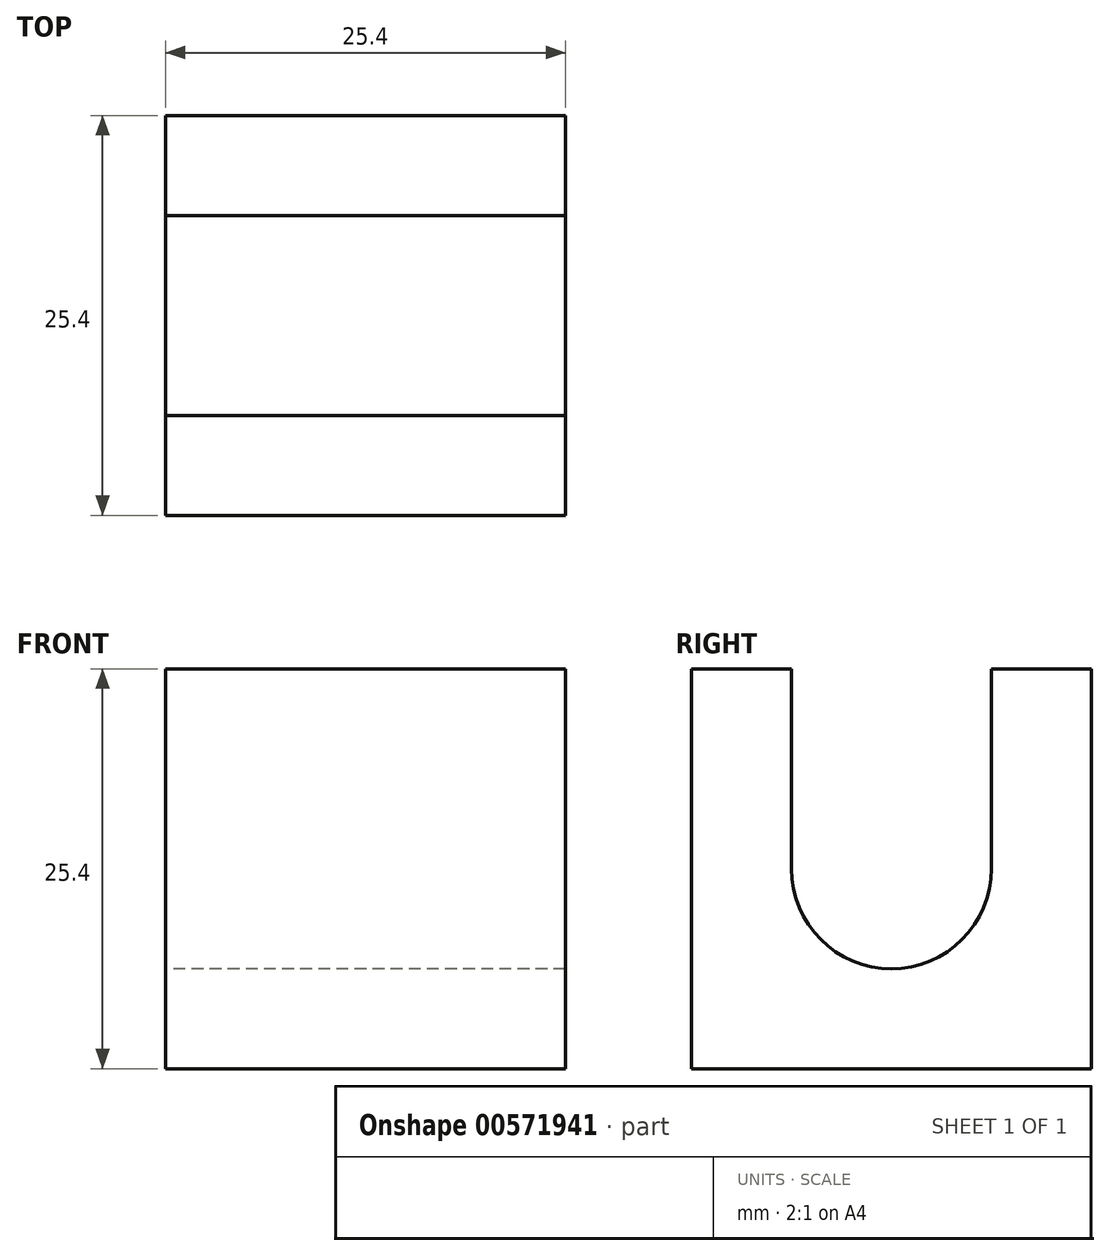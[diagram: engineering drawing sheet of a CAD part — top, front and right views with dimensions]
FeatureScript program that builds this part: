
annotation { "Feature Type Name" : "Feature", "Feature Type Description" : "" }
export const myFeature = defineFeature(function(context is Context, id is Id, definition is map)
    precondition{}
    {
        {
            var Q0;
            Q0=qCreatedBy(makeId("Right.planeOp"),FACE);
            var sketch = newSketch(context, id + "F0", { "sketchPlane" : qUnion([Q0])});
            skLineSegment(sketch, "E0.bottom", {"start": v(-21.4, 39.18) * mm, "end": v(4, 39.18) * mm});
            skLineSegment(sketch, "E0.top", {"start": v(-21.4, 13.78) * mm, "end": v(4, 13.78) * mm});
            skLineSegment(sketch, "E0.left", {"start": v(-21.4, 39.18) * mm, "end": v(-21.4, 13.78) * mm});
            skLineSegment(sketch, "E0.right", {"start": v(4, 39.18) * mm, "end": v(4, 13.78) * mm});
            skCircle(sketch, "E1", {"center": v(-8.7, 26.48) * mm, "radius": 6.35 * mm});
            skLineSegment(sketch, "E2", {"start": v(-2.36, 26.48) * mm, "end": v(-2.36, 39.18) * mm});
            skLineSegment(sketch, "E3", {"start": v(-15.06, 26.48) * mm, "end": v(-15.06, 39.18) * mm});
            skSolve(sketch);
        }
        {
            var Q0;
            Q0=makeQuery(id+"F0.imprint","IMPRINT",FACE,{"disambiguationData":[TD([[makeQuery(id+"F0.imprint","IMPRINT",EDGE,{"derivedFrom":sQuery(id+"F0.wireOp",EDGE,"E0.top")}),1.0]])]});
            extrude(context, id + "F1", {"entities" : qUnion([Q0]), "depth" : 25.4 * mm, "offsetDistance" : 25.4 * mm});
        }
    });
